# Revit family: IS_ConnectAir_E0734_BIM_DE
name_source: partatom
category: Plumbing Fixtures
revit_build: Autodesk Revit MEP 2014 (Build: 20130308_1515(x64)
units: mm (PartAtom-declared; Revit-internal decimal feet)

## types (2) — shared parameters
Accessories = www.idealstandard.de\ersatzteile
AreaUnits = millimeters
Assembly Code = C1030200
AssetType = Fixed
BREEAMApproved = No
Brand = Ideal Standard
CodePerformance = DIN EN 19542
ConnectionType = Plumbing
DurationUnit = year
ECA = No
ExpectedLife = 25
Features = Connect Air 4,5 litre cistern
GrossWeight = 0
IfcExportAs = IfcSanitaryTerminalType
IfcExportType = CISTERN
InstallationInstructions = www.idealstandard.de\produkte
LinearUnits = millimeters
ManufacturerURL = www.idealstandard.com
NBSDescription = WC cistern fittings
NBSReference = 45-30-70/387
NettWeight = 12,5 kg
NominalHeight = 381 mm
NominalLength = 178 mm
NominalWidth = 298 mm
ProductInformation = www.idealstandard.de/produkte
Shape = Sculptured
Size = 300x178x378mm
Space = Internal
ToiletPanType = WashDown
ToiletType = Other
URL = www.idealstandard.com
Version = 1
VolumeUnits = Litres
WRAS = No
WarrantyDescription = Manufacturers Warranty
WarrantyDurationUnit = year
WaterEfficientProduct = No
zero-valued in all types: CWFU, Cost, Default Elevation, HWFU, NominalDepth, SpilloverLevel, WFU

## per-type parameters (varying)
| type | BIMObjectName | BarCode | Description | Finish | Model | ModelNumber | ModelReference | Name |
| E073401 - Connect Air 4,5 litre cistern | ISI_IdealStandard__ConnectAir_E073401 | 5017830514633 | E073401 Connect Air 4,5 litre cistern | white | E073401 | E073401 |  | _ConnectAir_E073401_IdealStandard |
| E0734MA - Connect Air 4,5 litre cistern | ISI_IdealStandard__ConnectAir_E0734MA | 5017830521181 | E0734MA Connect Air 4,5 litre cistern | white with ideal plus | E0734MA | E0734MA | E0734MA Connect Air 4,5 litre cistern | _ConnectAir_E0734MA_IdealStandard |

## geometry (parser evidence)
native form markers: Sweep x8
no freeform markers — native parametric forms only
